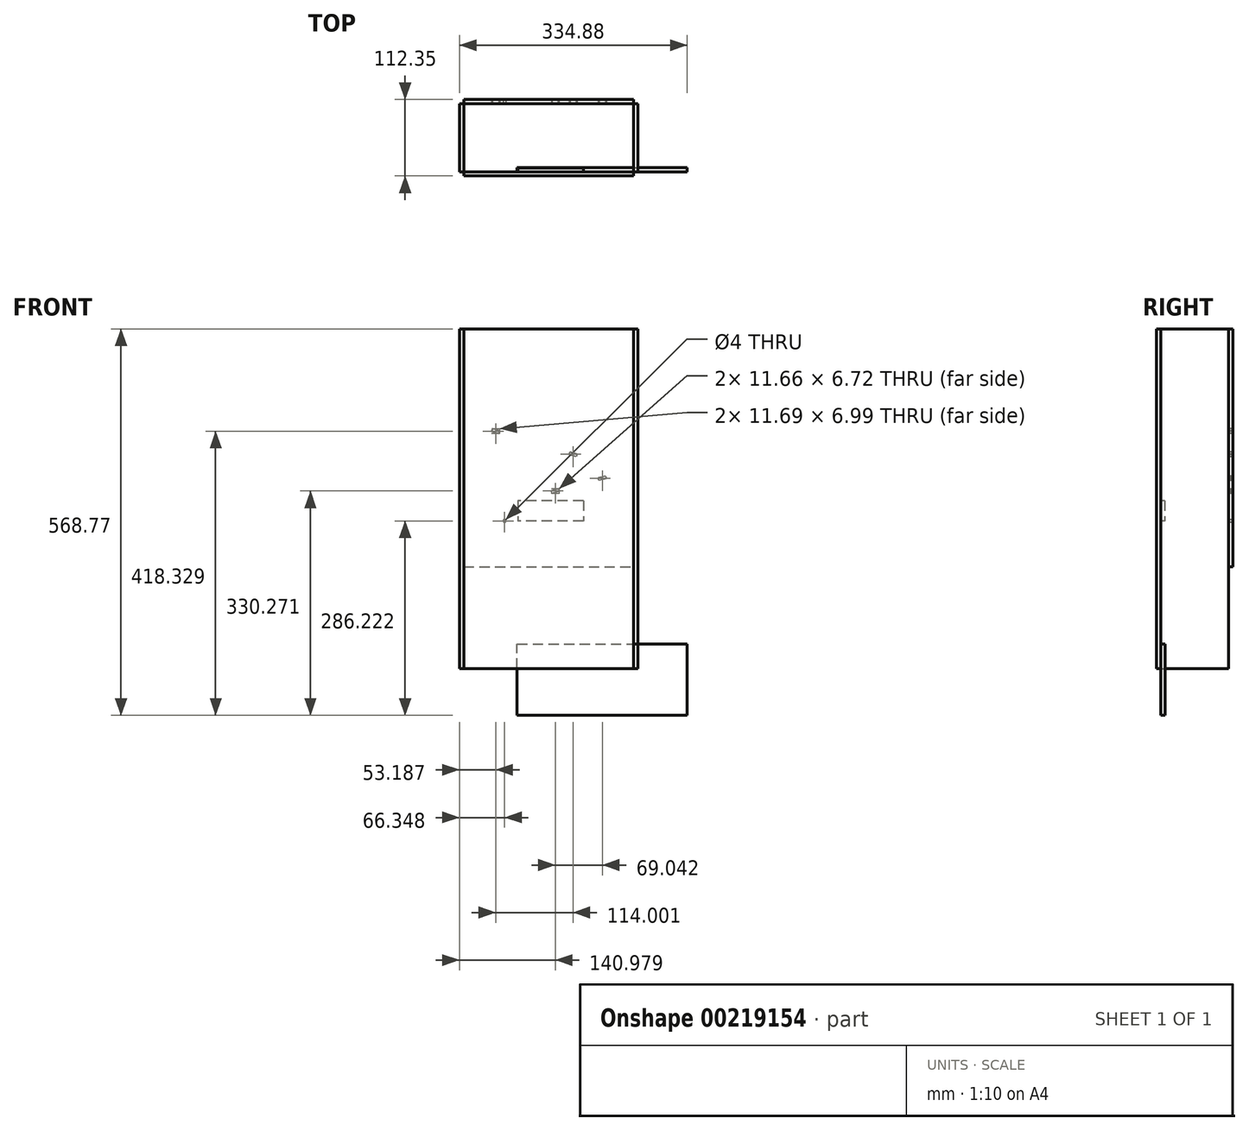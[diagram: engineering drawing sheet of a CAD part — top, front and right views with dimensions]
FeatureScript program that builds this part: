
annotation { "Feature Type Name" : "Feature", "Feature Type Description" : "" }
export const myFeature = defineFeature(function(context is Context, id is Id, definition is map)
    precondition{}
    {
        {
            var Q0;
            Q0=qCreatedBy(makeId("Front.planeOp"),FACE);
            var sketch = newSketch(context, id + "F0", { "sketchPlane" : qUnion([Q0])});
            skLineSegment(sketch, "E0.bottom", {"start": v(-134.22, 422.04) * mm, "end": v(115.78, 422.04) * mm});
            skLineSegment(sketch, "E0.top", {"start": v(-134.22, -77.96) * mm, "end": v(115.78, -77.96) * mm});
            skLineSegment(sketch, "E0.left", {"start": v(-134.22, 422.04) * mm, "end": v(-134.22, -77.96) * mm});
            skLineSegment(sketch, "E0.right", {"start": v(115.78, 422.04) * mm, "end": v(115.78, -77.96) * mm});
            skSolve(sketch);
        }
        {
            var Q0;
            Q0=sQuery(id+"F0.wireOp",EDGE,"E0.right");
            cPlane(context, id + "F1", {"entities" : qUnion([Q0]), "cplaneType" : CPlaneType.LINE_ANGLE, "offset" : 25.4 * mm, "angle" : 0 * degree, "width" : 152.4 * mm, "height" : 152.4 * mm});
        }
        {
            var Q0;
            Q0=makeQuery(id+"F0.imprint","IMPRINT",FACE,{"disambiguationData":[TD([[makeQuery(id+"F0.imprint","IMPRINT",EDGE,{"derivedFrom":sQuery(id+"F0.wireOp",EDGE,"E0.bottom")}),-1.0]])]});
            extrude(context, id + "F2", {"entities" : qUnion([Q0]), "depth" : 6 * mm});
        }
        {
            var Q0;
            Q0=makeQuery(id+"F2.opExtrude","CAP_EDGE",EDGE,{"disambiguationData":[OSD([sQuery(id+"F0.wireOp",EDGE,"E0.left")])],"isStart":false});
            cPoint(context, id + "F3", {"entities" : qUnion([Q0]), "parameter" : 0.5});
        }
        {
            var Q0;
            Q0=makeQuery(id+"F2.opExtrude","SWEPT_EDGE",EDGE,{"disambiguationData":[OSD([sQuery(id+"F0.wireOp",EDGE,"E0.bottom"),sQuery(id+"F0.wireOp",EDGE,"E0.left")])]});
            cPoint(context, id + "F4", {"entities" : qUnion([Q0]), "parameter" : 0.5});
        }
        {
            var Q0;
            Q0=makeQuery(id+"F2.opExtrude","CAP_VERTEX",VERTEX,{"disambiguationData":[OSD([sQuery(id+"F0.wireOp",EDGE,"E0.top"),sQuery(id+"F0.wireOp",EDGE,"E0.left")])],"isStart":false});
            var Q1;
            Q1 = qCreatedBy(id + "F3" ,VERTEX);
            var Q2;
            Q2 = qCreatedBy(id + "F4" ,VERTEX);
            cPlane(context, id + "F5", {"entities" : qUnion([Q0, Q1, Q2]), "cplaneType" : CPlaneType.THREE_POINT, "offset" : 25.4 * mm, "width" : 152.4 * mm, "height" : 152.4 * mm});
        }
        {
            var Q0;
            Q0=qCreatedBy(id+"F5.planeOp",FACE);
            var sketch = newSketch(context, id + "F6", { "sketchPlane" : qUnion([Q0])});
            skLineSegment(sketch, "E1.bottom", {"start": v(12.15, 414.38) * mm, "end": v(112.15, 414.38) * mm});
            skLineSegment(sketch, "E1.top", {"start": v(12.15, -85.62) * mm, "end": v(112.15, -85.62) * mm});
            skLineSegment(sketch, "E1.left", {"start": v(12.15, 414.38) * mm, "end": v(12.15, -85.62) * mm});
            skLineSegment(sketch, "E1.right", {"start": v(112.15, 414.38) * mm, "end": v(112.15, -85.62) * mm});
            skSolve(sketch);
        }
        {
            var Q0;
            Q0=qCreatedBy(id+"F1.planeOp",FACE);
            var sketch = newSketch(context, id + "F7", { "sketchPlane" : qUnion([Q0])});
            skLineSegment(sketch, "E2.bottom", {"start": v(0, 436.44) * mm, "end": v(-100, 436.44) * mm});
            skLineSegment(sketch, "E2.top", {"start": v(0, -63.56) * mm, "end": v(-100, -63.56) * mm});
            skLineSegment(sketch, "E2.left", {"start": v(0, 436.44) * mm, "end": v(0, -63.56) * mm});
            skLineSegment(sketch, "E2.right", {"start": v(-100, 436.44) * mm, "end": v(-100, -63.56) * mm});
            skSolve(sketch);
        }
        {
            var Q0;
            Q0=makeQuery(id+"F7.imprint","IMPRINT",FACE,{"disambiguationData":[TD([[makeQuery(id+"F7.imprint","IMPRINT",EDGE,{"derivedFrom":sQuery(id+"F7.wireOp",EDGE,"E2.bottom")}),1.0]])]});
            extrude(context, id + "F8", {"entities" : qUnion([Q0]), "operationType" : NewBodyOperationType.ADD, "oppositeDirection" : true, "depth" : 6 * mm});
        }
        {
            var Q0;
            Q0 = qSketchRegion(id + "F6", true);
            extrude(context, id + "F9", {"entities" : qUnion([Q0]), "oppositeDirection" : true, "depth" : 6.35 * mm});
        }
        {
            var Q0;
            Q0=makeQuery(id+"F9.opExtrude","SWEPT_BODY",BODY,{"disambiguationData":[OSD([sQuery(id+"F6.wireOp",EDGE,"E1.bottom"),sQuery(id+"F6.wireOp",EDGE,"E1.top"),sQuery(id+"F6.wireOp",EDGE,"E1.left"),sQuery(id+"F6.wireOp",EDGE,"E1.right")])]});
            var Q1;
            Q1=makeQuery(id+"F9.opExtrude","CAP_VERTEX",VERTEX,{"disambiguationData":[OSD([sQuery(id+"F6.wireOp",EDGE,"E1.bottom"),sQuery(id+"F6.wireOp",EDGE,"E1.left")])],"isStart":true});
            var Q2;
            Q2=makeQuery(id+"F2.opExtrude","CAP_VERTEX",VERTEX,{"disambiguationData":[OSD([sQuery(id+"F0.wireOp",EDGE,"E0.bottom"),sQuery(id+"F0.wireOp",EDGE,"E0.left")])],"isStart":true});
            transform(context, id + "F10", {"entities" : qUnion([Q0]), "transformType" : TransformType.TRANSLATION_ENTITY, "oppositeDirectionEntity" : false, "transformLine" : qUnion([Q1, Q2]), "makeCopy" : false});
        }
        {
            var Q0;
            Q0=makeQuery(id+"F8.opExtrude","CAP_EDGE",EDGE,{"disambiguationData":[OSD([sQuery(id+"F7.wireOp",EDGE,"E2.right")])],"isStart":true});
            var Q1;
            Q1=makeQuery(id+"F8.opExtrude","CAP_EDGE",EDGE,{"disambiguationData":[OSD([sQuery(id+"F7.wireOp",EDGE,"E2.right")])],"isStart":false});
            cPlane(context, id + "F11", {"entities" : qUnion([Q0, Q1]), "cplaneType" : CPlaneType.LINE_ANGLE, "offset" : 25.4 * mm, "angle" : 0 * degree, "width" : 152.4 * mm, "height" : 152.4 * mm});
        }
        {
            var Q0;
            Q0=qCreatedBy(id+"F11.planeOp",FACE);
            var sketch = newSketch(context, id + "F12", { "sketchPlane" : qUnion([Q0])});
            skLineSegment(sketch, "E3.bottom", {"start": v(-134.22, 422.04) * mm, "end": v(115.78, 422.04) * mm});
            skLineSegment(sketch, "E3.top", {"start": v(-134.22, 72.04) * mm, "end": v(115.78, 72.04) * mm});
            skLineSegment(sketch, "E3.left", {"start": v(-134.22, 422.04) * mm, "end": v(-134.22, 72.04) * mm});
            skLineSegment(sketch, "E3.right", {"start": v(115.78, 422.04) * mm, "end": v(115.78, 72.04) * mm});
            skLineSegment(sketch, "E4", {"start": v(-92.08, 275.1) * mm, "end": v(-93.23, 271.26) * mm});
            skLineSegment(sketch, "E5", {"start": v(-93.23, 271.26) * mm, "end": v(-82.69, 268.1) * mm});
            skLineSegment(sketch, "E6", {"start": v(-82.69, 268.1) * mm, "end": v(-81.54, 271.94) * mm});
            skLineSegment(sketch, "E7", {"start": v(32.46, 237.8) * mm, "end": v(31.31, 233.98) * mm});
            skLineSegment(sketch, "E8", {"start": v(31.31, 233.98) * mm, "end": v(20.78, 237.13) * mm});
            skLineSegment(sketch, "E9", {"start": v(20.78, 237.13) * mm, "end": v(21.92, 240.96) * mm});
            skLineSegment(sketch, "E10", {"start": v(74.24, 205.49) * mm, "end": v(75.28, 201.63) * mm});
            skLineSegment(sketch, "E11", {"start": v(75.28, 201.63) * mm, "end": v(64.66, 198.77) * mm});
            skLineSegment(sketch, "E12", {"start": v(64.66, 198.77) * mm, "end": v(63.62, 202.63) * mm});
            skLineSegment(sketch, "E13", {"start": v(74.24, 205.49) * mm, "end": v(63.62, 202.63) * mm});
            skLineSegment(sketch, "E14", {"start": v(32.46, 237.8) * mm, "end": v(21.92, 240.96) * mm});
            skLineSegment(sketch, "E15", {"start": v(-81.54, 271.94) * mm, "end": v(-92.08, 275.1) * mm});
            skLineSegment(sketch, "E16", {"start": v(5.2, 186.9) * mm, "end": v(6.24, 183.04) * mm});
            skLineSegment(sketch, "E17", {"start": v(6.24, 183.04) * mm, "end": v(-4.38, 180.18) * mm});
            skLineSegment(sketch, "E18", {"start": v(-4.38, 180.18) * mm, "end": v(-5.42, 184.04) * mm});
            skLineSegment(sketch, "E19", {"start": v(5.2, 186.9) * mm, "end": v(-5.42, 184.04) * mm});
            skCircle(sketch, "E20", {"center": v(-74.22, 139.5) * mm, "radius": 2 * mm});
            skSolve(sketch);
        }
        {
            var Q0;
            Q0 = qSketchRegion(id + "F12", true);
            extrude(context, id + "F13", {"entities" : qUnion([Q0]), "oppositeDirection" : true, "depth" : 6.35 * mm});
        }
        {
            var Q0;
            Q0=makeQuery(id+"F2.opExtrude","CAP_EDGE",EDGE,{"disambiguationData":[OSD([sQuery(id+"F0.wireOp",EDGE,"E0.bottom")])],"isStart":true});
            var Q1;
            Q1=makeQuery(id+"F13.opExtrude","CAP_EDGE",EDGE,{"disambiguationData":[OSD([sQuery(id+"FXKDgHbDaSFVtWv_5.wireOp",EDGE,"Z1vdWbhB-fxrM-UTgv-NkZF-OY8Rp6UQyxRM.bottom")])],"isStart":true});
            cPlane(context, id + "F14", {"entities" : qUnion([Q0, Q1]), "cplaneType" : CPlaneType.LINE_ANGLE, "offset" : 25.4 * mm, "angle" : 0 * degree, "width" : 152.4 * mm, "height" : 152.4 * mm});
        }
        {
            var Q0;
            Q0=qCreatedBy(id+"F14.planeOp",FACE);
            var sketch = newSketch(context, id + "F15", { "sketchPlane" : qUnion([Q0])});
            skLineSegment(sketch, "E21.bottom", {"start": v(55.7, -146.73) * mm, "end": v(-194.3, -146.73) * mm});
            skLineSegment(sketch, "E21.top", {"start": v(55.7, -41.73) * mm, "end": v(-194.3, -41.73) * mm});
            skLineSegment(sketch, "E21.left", {"start": v(55.7, -146.73) * mm, "end": v(55.7, -41.73) * mm});
            skLineSegment(sketch, "E21.right", {"start": v(-194.3, -146.73) * mm, "end": v(-194.3, -41.73) * mm});
            skSolve(sketch);
        }
        {
            var Q0;
            Q0=makeQuery(id+"F15.imprint","IMPRINT",FACE,{"disambiguationData":[TD([[makeQuery(id+"F15.imprint","IMPRINT",EDGE,{"derivedFrom":sQuery(id+"F15.wireOp",EDGE,"E21.bottom")}),-1.0]])]});
            extrude(context, id + "F16", {"entities" : qUnion([Q0]), "depth" : 6.35 * mm});
        }
        {
            var Q0;
            Q0=qCreatedBy(id+"F14.planeOp",FACE);
            var sketch = newSketch(context, id + "F17", { "sketchPlane" : qUnion([Q0])});
            skLineSegment(sketch, "E22.bottom", {"start": v(-41.5, 169.42) * mm, "end": v(54.5, 169.42) * mm});
            skLineSegment(sketch, "E22.top", {"start": v(-41.5, 139.42) * mm, "end": v(54.5, 139.42) * mm});
            skLineSegment(sketch, "E22.left", {"start": v(-41.5, 169.42) * mm, "end": v(-41.5, 139.42) * mm});
            skLineSegment(sketch, "E22.right", {"start": v(54.5, 169.42) * mm, "end": v(54.5, 139.42) * mm});
            skSolve(sketch);
        }
        {
            var Q0;
            Q0 = qSketchRegion(id + "F17", true);
            extrude(context, id + "F18", {"entities" : qUnion([Q0]), "depth" : 6 * mm});
        }
        {
            var Q0;
            Q0=makeQuery(id+"F8.opExtrude","SWEPT_BODY",BODY,{"disambiguationData":[OSD([sQuery(id+"F7.wireOp",EDGE,"E2.bottom"),sQuery(id+"F7.wireOp",EDGE,"E2.top"),sQuery(id+"F7.wireOp",EDGE,"E2.left"),sQuery(id+"F7.wireOp",EDGE,"E2.right")])]});
            var Q1;
            Q1=makeQuery(id+"F8.opExtrude","CAP_VERTEX",VERTEX,{"disambiguationData":[OSD([sQuery(id+"F7.wireOp",EDGE,"E2.bottom"),sQuery(id+"F7.wireOp",EDGE,"E2.left")])],"isStart":true});
            var Q2;
            Q2=makeQuery(id+"F2.opExtrude","CAP_VERTEX",VERTEX,{"disambiguationData":[OSD([sQuery(id+"F0.wireOp",EDGE,"E0.bottom"),sQuery(id+"F0.wireOp",EDGE,"E0.right")])],"isStart":true});
            transform(context, id + "F19", {"entities" : qUnion([Q0]), "transformType" : TransformType.TRANSLATION_ENTITY, "oppositeDirectionEntity" : false, "transformLine" : qUnion([Q1, Q2]), "makeCopy" : false});
        }
    });
